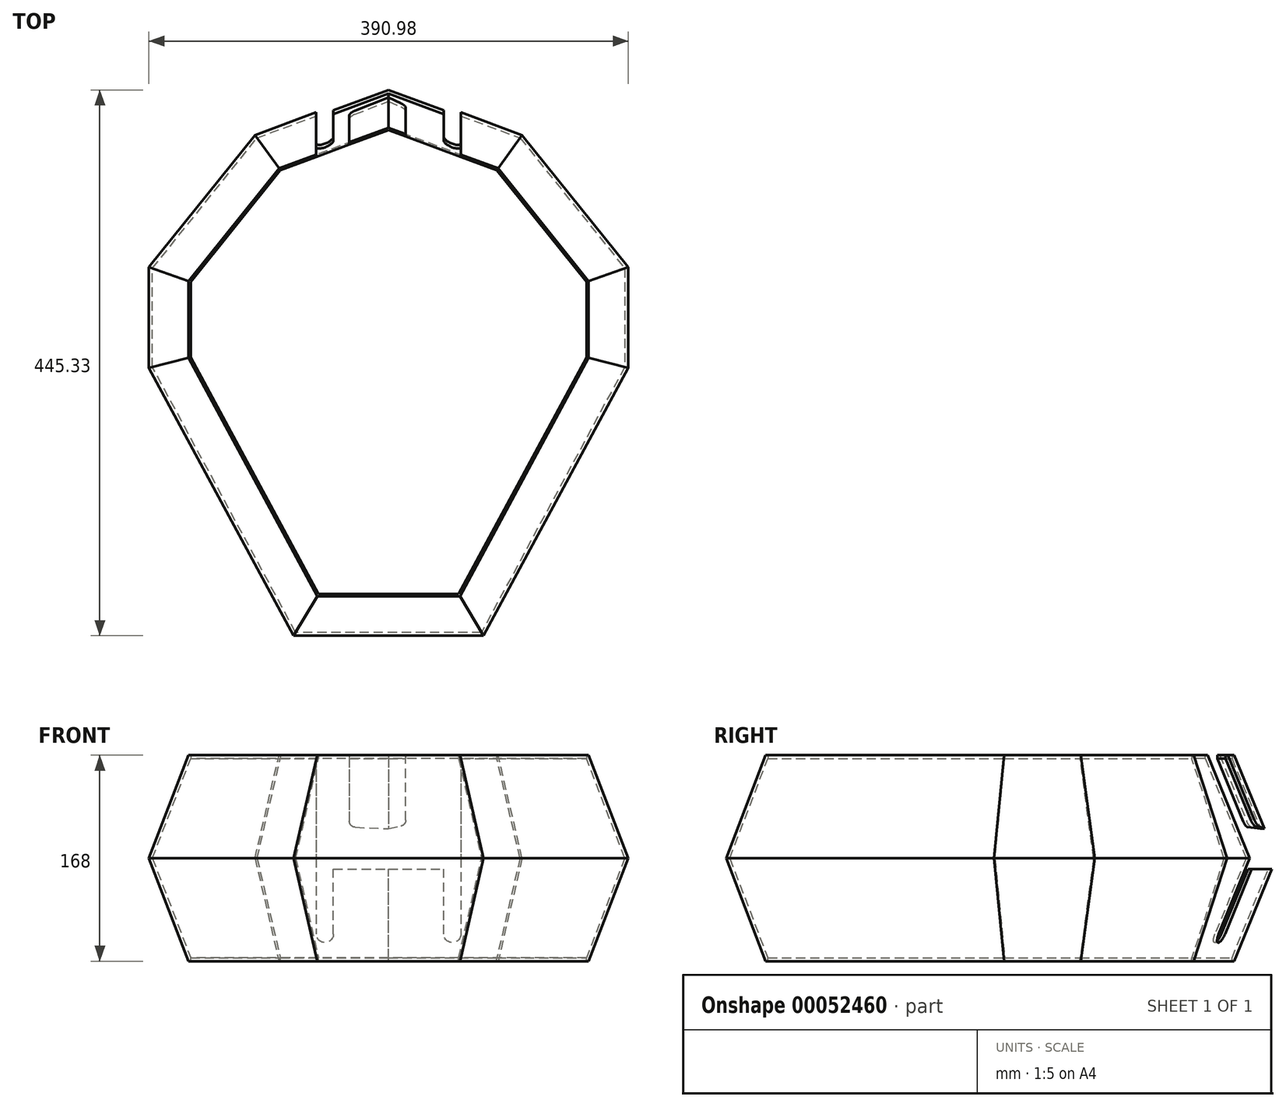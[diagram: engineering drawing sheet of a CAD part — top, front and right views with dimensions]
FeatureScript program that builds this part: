
annotation { "Feature Type Name" : "Feature", "Feature Type Description" : "" }
export const myFeature = defineFeature(function(context is Context, id is Id, definition is map)
    precondition{}
    {
        {
            var Q0;
            Q0=qCreatedBy(makeId("Top.planeOp"),FACE);
            var sketch = newSketch(context, id + "F0", { "sketchPlane" : qUnion([Q0])});
            skLineSegment(sketch, "E0", {"start": v(0, 182.08) * mm, "end": v(-89.4, 148.98) * mm});
            skLineSegment(sketch, "E1", {"start": v(-89.4, 148.98) * mm, "end": v(-163.25, 56.94) * mm});
            skLineSegment(sketch, "E2", {"start": v(-163.25, 56.94) * mm, "end": v(-163.25, -5.76) * mm});
            skLineSegment(sketch, "E3", {"start": v(-163.25, -5.76) * mm, "end": v(-58.25, -200.22) * mm});
            skLineSegment(sketch, "E4", {"start": v(-58.25, -200.22) * mm, "end": v(0, -200.22) * mm});
            skLineSegment(sketch, "E5", {"start": v(0, 281.24) * mm, "end": v(0, -282.32) * mm, "construction": true});
            skLineSegment(sketch, "E6.MirrorCS", {"start": v(0, 182.08) * mm, "end": v(89.4, 148.98) * mm});
            skLineSegment(sketch, "E7.MirrorCS", {"start": v(89.4, 148.98) * mm, "end": v(163.25, 56.94) * mm});
            skLineSegment(sketch, "E8.MirrorCS", {"start": v(163.25, 56.94) * mm, "end": v(163.25, -5.76) * mm});
            skLineSegment(sketch, "E9.MirrorCS", {"start": v(163.25, -5.76) * mm, "end": v(58.25, -200.22) * mm});
            skLineSegment(sketch, "E10.MirrorCS", {"start": v(58.25, -200.22) * mm, "end": v(0, -200.22) * mm});
            skSolve(sketch);
        }
        {
            var Q0;
            Q0=makeQuery(id+"F0.imprint","IMPRINT",FACE,{"disambiguationData":[TD([[makeQuery(id+"F0.imprint","IMPRINT",EDGE,{"derivedFrom":sQuery(id+"F0.wireOp",EDGE,"E0")}),1.0]])]});
            extrude(context, id + "F1", {"entities" : qUnion([Q0]), "depth" : 84 * mm, "hasDraft" : true, "draftAngle" : 21 * degree});
        }
        {
            var Q0;
            Q0=makeQuery(id+"F1.opExtrude","CAP_FACE",FACE,{"disambiguationData":[OSD([sQuery(id+"F0.wireOp",EDGE,"E0"),sQuery(id+"F0.wireOp",EDGE,"E1"),sQuery(id+"F0.wireOp",EDGE,"E2"),sQuery(id+"F0.wireOp",EDGE,"E3"),sQuery(id+"F0.wireOp",EDGE,"E4"),sQuery(id+"F0.wireOp",EDGE,"E6.MirrorCS"),sQuery(id+"F0.wireOp",EDGE,"E7.MirrorCS"),sQuery(id+"F0.wireOp",EDGE,"E8.MirrorCS"),sQuery(id+"F0.wireOp",EDGE,"E9.MirrorCS"),sQuery(id+"F0.wireOp",EDGE,"E10.MirrorCS")])],"isStart":false});
            shell(context, id + "F2", {"entities" : qUnion([Q0]), "thickness" : 2.6 * mm});
        }
        {
            var Q0;
            Q0=makeQuery(id+"F2.opShell","OFFSET_FACE",FACE,{"disambiguationData":[OSD([sQuery(id+"F0.wireOp",EDGE,"E0"),sQuery(id+"F0.wireOp",EDGE,"E1"),sQuery(id+"F0.wireOp",EDGE,"E2"),sQuery(id+"F0.wireOp",EDGE,"E3"),sQuery(id+"F0.wireOp",EDGE,"E4"),sQuery(id+"F0.wireOp",EDGE,"E6.MirrorCS"),sQuery(id+"F0.wireOp",EDGE,"E7.MirrorCS"),sQuery(id+"F0.wireOp",EDGE,"E8.MirrorCS"),sQuery(id+"F0.wireOp",EDGE,"E9.MirrorCS"),sQuery(id+"F0.wireOp",EDGE,"E10.MirrorCS")])]});
            extrude(context, id + "F3", {"entities" : qUnion([Q0]), "operationType" : NewBodyOperationType.REMOVE, "oppositeDirection" : true, "depth" : 25 * mm});
        }
        {
            var Q0;
            Q0=makeQuery(id+"F1.opExtrude","SWEPT_BODY",BODY,{"disambiguationData":[OSD([sQuery(id+"F0.wireOp",EDGE,"E0"),sQuery(id+"F0.wireOp",EDGE,"E1"),sQuery(id+"F0.wireOp",EDGE,"E2"),sQuery(id+"F0.wireOp",EDGE,"E3"),sQuery(id+"F0.wireOp",EDGE,"E4"),sQuery(id+"F0.wireOp",EDGE,"E6.MirrorCS"),sQuery(id+"F0.wireOp",EDGE,"E7.MirrorCS"),sQuery(id+"F0.wireOp",EDGE,"E8.MirrorCS"),sQuery(id+"F0.wireOp",EDGE,"E9.MirrorCS"),sQuery(id+"F0.wireOp",EDGE,"E10.MirrorCS")])]});
            transform(context, id + "F4", {"entities" : qUnion([Q0]), "transformType" : TransformType.TRANSLATION_3D, "dx" : 0 * mm, "dy" : 0 * mm, "dz" : 153.94 * mm, "makeCopy" : true});
        }
        {
            var Q0;
            Q0=makeQuery(id+"F1.opExtrude","SWEPT_BODY",BODY,{"disambiguationData":[OSD([sQuery(id+"F0.wireOp",EDGE,"E0"),sQuery(id+"F0.wireOp",EDGE,"E1"),sQuery(id+"F0.wireOp",EDGE,"E2"),sQuery(id+"F0.wireOp",EDGE,"E3"),sQuery(id+"F0.wireOp",EDGE,"E4"),sQuery(id+"F0.wireOp",EDGE,"E6.MirrorCS"),sQuery(id+"F0.wireOp",EDGE,"E7.MirrorCS"),sQuery(id+"F0.wireOp",EDGE,"E8.MirrorCS"),sQuery(id+"F0.wireOp",EDGE,"E9.MirrorCS"),sQuery(id+"F0.wireOp",EDGE,"E10.MirrorCS")])]});
            var Q1;
            Q1=makeQuery(id+"F1.opExtrude","CAP_FACE",FACE,{"disambiguationData":[OSD([sQuery(id+"F0.wireOp",EDGE,"E0"),sQuery(id+"F0.wireOp",EDGE,"E1"),sQuery(id+"F0.wireOp",EDGE,"E2"),sQuery(id+"F0.wireOp",EDGE,"E3"),sQuery(id+"F0.wireOp",EDGE,"E4"),sQuery(id+"F0.wireOp",EDGE,"E6.MirrorCS"),sQuery(id+"F0.wireOp",EDGE,"E7.MirrorCS"),sQuery(id+"F0.wireOp",EDGE,"E8.MirrorCS"),sQuery(id+"F0.wireOp",EDGE,"E9.MirrorCS"),sQuery(id+"F0.wireOp",EDGE,"E10.MirrorCS")])],"isStart":false});
            var Q2;
            Q2=makeQuery(id+"F1.opExtrude","CAP_FACE",FACE,{"disambiguationData":[OSD([sQuery(id+"F0.wireOp",EDGE,"E0"),sQuery(id+"F0.wireOp",EDGE,"E1"),sQuery(id+"F0.wireOp",EDGE,"E2"),sQuery(id+"F0.wireOp",EDGE,"E3"),sQuery(id+"F0.wireOp",EDGE,"E4"),sQuery(id+"F0.wireOp",EDGE,"E6.MirrorCS"),sQuery(id+"F0.wireOp",EDGE,"E7.MirrorCS"),sQuery(id+"F0.wireOp",EDGE,"E8.MirrorCS"),sQuery(id+"F0.wireOp",EDGE,"E9.MirrorCS"),sQuery(id+"F0.wireOp",EDGE,"E10.MirrorCS")])],"isStart":false});
            mirror(context, id + "F5", {"entities" : qUnion([Q0]), "faces" : qUnion([Q1]), "mirrorPlane" : qUnion([Q2])});
        }
        {
            var Q0;
            Q0=makeQuery(id+"F4.opPattern","COPY",BODY,{"derivedFrom":makeQuery(id+"F1.opExtrude","SWEPT_BODY",BODY,{"disambiguationData":[OSD([sQuery(id+"F0.wireOp",EDGE,"E0"),sQuery(id+"F0.wireOp",EDGE,"E1"),sQuery(id+"F0.wireOp",EDGE,"E2"),sQuery(id+"F0.wireOp",EDGE,"E3"),sQuery(id+"F0.wireOp",EDGE,"E4"),sQuery(id+"F0.wireOp",EDGE,"E6.MirrorCS"),sQuery(id+"F0.wireOp",EDGE,"E7.MirrorCS"),sQuery(id+"F0.wireOp",EDGE,"E8.MirrorCS"),sQuery(id+"F0.wireOp",EDGE,"E9.MirrorCS"),sQuery(id+"F0.wireOp",EDGE,"E10.MirrorCS")])]}),"instanceName":"1"});
            deleteBodies(context, id + "F6", {"entities" : qUnion([Q0])});
        }
        {
            var Q0;
            Q0=qCreatedBy(makeId("Front.planeOp"),FACE);
            var sketch = newSketch(context, id + "F7", { "sketchPlane" : qUnion([Q0])});
            skCircle(sketch, "E11", {"center": v(52, 22.13) * mm, "radius": 7 * mm});
            skLineSegment(sketch, "E12", {"start": v(59, 22.13) * mm, "end": v(59, 192.13) * mm});
            skLineSegment(sketch, "E13", {"start": v(59, 192.13) * mm, "end": v(45, 192.13) * mm});
            skLineSegment(sketch, "E14", {"start": v(45, 192.13) * mm, "end": v(45, 22.13) * mm});
            skLineSegment(sketch, "E15", {"start": v(0, 236.77) * mm, "end": v(0, -122.19) * mm, "construction": true});
            skLineSegment(sketch, "E16", {"start": v(-261.72, 0) * mm, "end": v(397.78, 0) * mm, "construction": true});
            skLineSegment(sketch, "E17.MirrorCS", {"start": v(-45, 192.13) * mm, "end": v(-45, 22.13) * mm});
            skLineSegment(sketch, "E18.MirrorCS", {"start": v(-59, 192.13) * mm, "end": v(-45, 192.13) * mm});
            skLineSegment(sketch, "E19.MirrorCS", {"start": v(-59, 22.13) * mm, "end": v(-59, 192.13) * mm});
            skCircle(sketch, "E20.MirrorC", {"center": v(-52, 22.13) * mm, "radius": 7 * mm});
            skSolve(sketch);
        }
        {
            var Q0;
            Q0 = qSketchRegion(id + "F7", true);
            extrude(context, id + "F8", {"entities" : qUnion([Q0]), "operationType" : NewBodyOperationType.REMOVE, "oppositeDirection" : true, "depth" : 276.5 * mm});
        }
        {
            var Q0;
            Q0=qCreatedBy(makeId("Front.planeOp"),FACE);
            var sketch = newSketch(context, id + "F9", { "sketchPlane" : qUnion([Q0])});
            skLineSegment(sketch, "E21", {"start": v(0, 390.04) * mm, "end": v(0, -284.23) * mm, "construction": true});
            skLineSegment(sketch, "E22", {"start": v(-393.14, 0) * mm, "end": v(501.65, 0) * mm, "construction": true});
            skLineSegment(sketch, "E23", {"start": v(0, 199.66) * mm, "end": v(0, 108) * mm});
            skLineSegment(sketch, "E24", {"start": v(0, 108) * mm, "end": v(-32, 109.5) * mm});
            skLineSegment(sketch, "E25", {"start": v(-32, 109.5) * mm, "end": v(-32, 199.66) * mm});
            skLineSegment(sketch, "E26", {"start": v(14, 199.66) * mm, "end": v(14, 111.01) * mm});
            skLineSegment(sketch, "E27", {"start": v(14, 111.01) * mm, "end": v(0, 108) * mm});
            skLineSegment(sketch, "E28", {"start": v(-32, 199.66) * mm, "end": v(-51.6, 199.66) * mm});
            skLineSegment(sketch, "E29", {"start": v(-51.6, 199.66) * mm, "end": v(-51.6, 109.5) * mm});
            skLineSegment(sketch, "E30", {"start": v(-51.6, 109.5) * mm, "end": v(-32, 109.5) * mm});
            skLineSegment(sketch, "E31", {"start": v(14, 199.66) * mm, "end": v(53.16, 199.66) * mm});
            skLineSegment(sketch, "E32", {"start": v(53.16, 199.66) * mm, "end": v(53.16, 75.21) * mm});
            skLineSegment(sketch, "E33", {"start": v(53.16, 75.21) * mm, "end": v(0, 75.21) * mm});
            skLineSegment(sketch, "E34", {"start": v(0, 75.21) * mm, "end": v(0, 108) * mm});
            skLineSegment(sketch, "E35", {"start": v(-51.6, 109.5) * mm, "end": v(-51.6, 75.21) * mm});
            skLineSegment(sketch, "E36", {"start": v(-51.6, 75.21) * mm, "end": v(0, 75.21) * mm});
            skSolve(sketch);
        }
        {
            var Q0;
            Q0 = qSketchRegion(id + "F9", true);
            extrude(context, id + "F10", {"entities" : qUnion([Q0]), "operationType" : NewBodyOperationType.REMOVE, "oppositeDirection" : true, "depth" : 300 * mm});
        }
        {
            var Q0;
            Q0=makeQuery(id+"F10.boolean.opBoolean","COPY",EDGE,{"derivedFrom":makeQuery(id+"F10.opExtrude","SWEPT_EDGE",EDGE,{"disambiguationData":[OSD([sQuery(id+"F9.wireOp",EDGE,"E26"),sQuery(id+"F9.wireOp",EDGE,"E27")])]})});
            var Q1;
            Q1=makeQuery(id+"F10.boolean.opBoolean","COPY",EDGE,{"derivedFrom":makeQuery(id+"F10.opExtrude","SWEPT_EDGE",EDGE,{"disambiguationData":[OSD([sQuery(id+"F9.wireOp",EDGE,"E24"),sQuery(id+"F9.wireOp",EDGE,"E25")])]})});
            fillet(context, id + "F11", {"entities" : qUnion([Q0, Q1]), "radius" : 5 * mm, "allowEdgeOverflow" : false});
        }
    });
